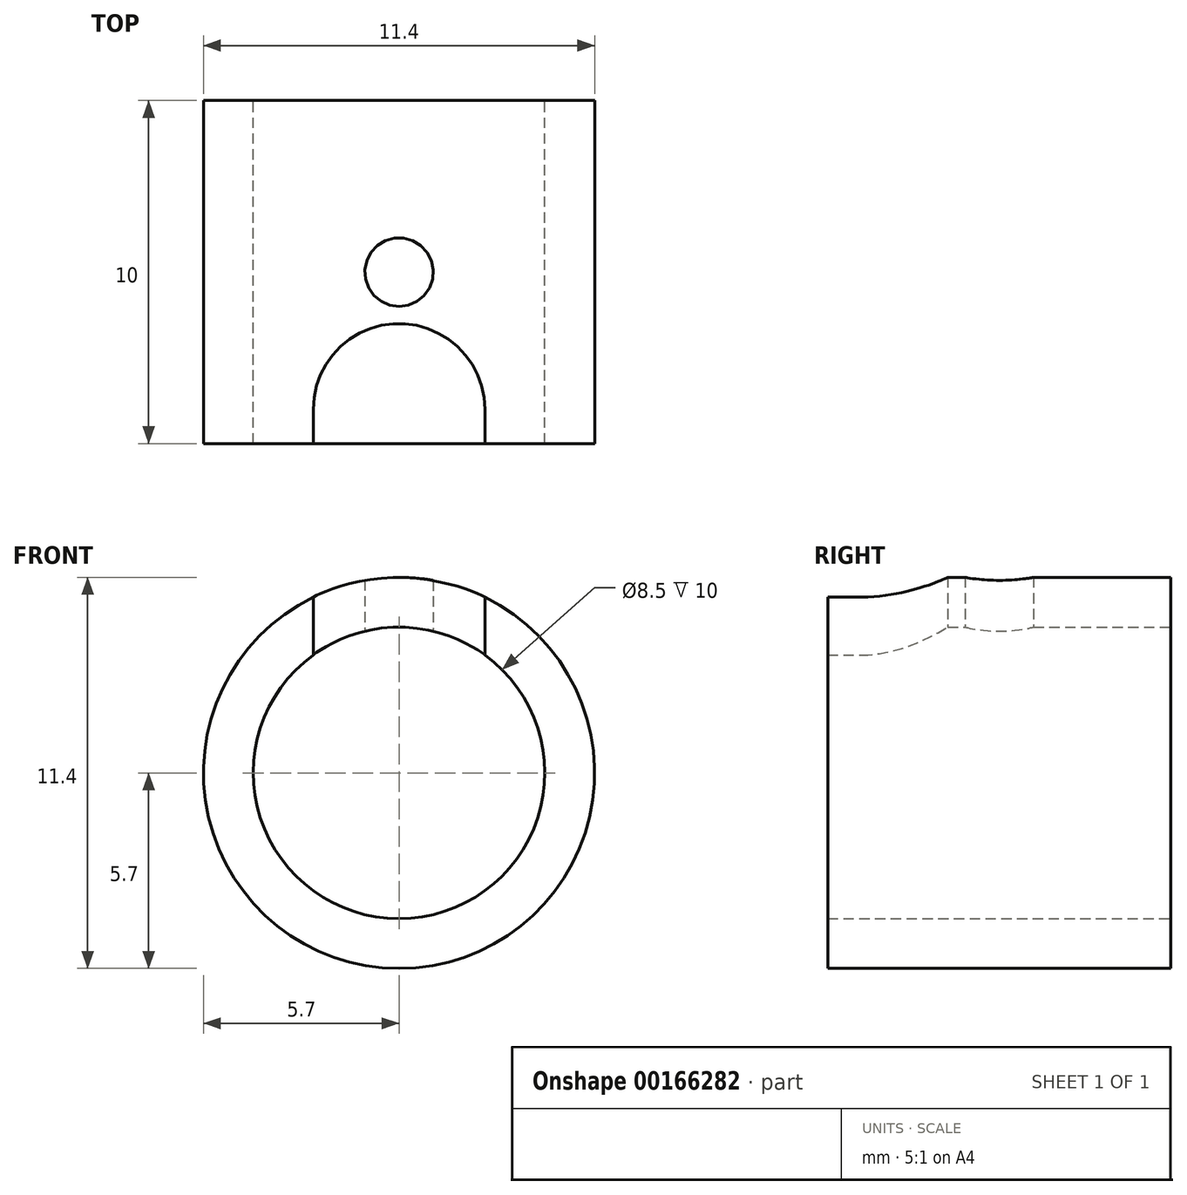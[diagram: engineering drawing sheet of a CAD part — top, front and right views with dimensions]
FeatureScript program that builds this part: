
annotation { "Feature Type Name" : "Feature", "Feature Type Description" : "" }
export const myFeature = defineFeature(function(context is Context, id is Id, definition is map)
    precondition{}
    {
        {
            assignVariable(context, id + "F0", {"name" : "Main_Length", "anyValue" : 10});
        }
        {
            var Q0;
            Q0=qCreatedBy(makeId("Front.planeOp"),FACE);
            var sketch = newSketch(context, id + "F1", { "sketchPlane" : qUnion([Q0])});
            skCircle(sketch, "E0", {"center": v(0, 0) * mm, "radius": 5.7 * mm});
            skCircle(sketch, "E1", {"center": v(0, 0) * mm, "radius": 4.25 * mm});
            skSolve(sketch);
        }
        {
            var Q0;
            Q0=makeQuery(id+"F1.imprint","IMPRINT",FACE,{"disambiguationData":[TD([[makeQuery(id+"F1.imprint","IMPRINT",EDGE,{"derivedFrom":sQuery(id+"F1.wireOp",EDGE,"E0")}),1.0]])]});
            extrude(context, id + "F2", {"entities" : qUnion([Q0]), "depth" : (getVariable(context, 'Main_Length')) * mm});
        }
        {
            var Q0;
            Q0=qCreatedBy(makeId("Top.planeOp"),FACE);
            var sketch = newSketch(context, id + "F3", { "sketchPlane" : qUnion([Q0])});
            skArc(sketch, "E2", {"start": v(2.5, -9) * mm, "mid": v(0, -6.5) * mm, "end": v(-2.5, -9) * mm});
            skLineSegment(sketch, "E3", {"start": v(-2.5, -9) * mm, "end": v(-2.5, -10) * mm});
            skLineSegment(sketch, "E4", {"start": v(2.5, -9) * mm, "end": v(2.5, -10) * mm});
            skLineSegment(sketch, "E5.0", {"start": v(5.7, -10) * mm, "end": v(-5.7, -10) * mm});
            skCircle(sketch, "E6", {"center": v(0, -5) * mm, "radius": 1 * mm});
            skSolve(sketch);
        }
        {
            var Q0;
            Q0=makeQuery(id+"F3.imprint","IMPRINT",FACE,{"disambiguationData":[TD([[makeQuery(id+"F3.imprint","IMPRINT",EDGE,{"derivedFrom":sQuery(id+"F3.wireOp",EDGE,"E6")}),1.0]])]});
            var Q1;
            Q1=makeQuery(id+"F3.imprint","IMPRINT",FACE,{"disambiguationData":[TD([[makeQuery(id+"F3.imprint","IMPRINT",EDGE,{"derivedFrom":sQuery(id+"F3.wireOp",EDGE,"E2")}),1.0]])]});
            extrude(context, id + "F4", {"entities" : qUnion([Q0, Q1]), "operationType" : NewBodyOperationType.REMOVE, "endBound" : BoundingType.THROUGH_ALL, "depth" : 25 * mm});
        }
    });
